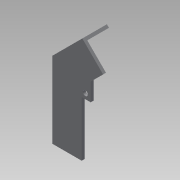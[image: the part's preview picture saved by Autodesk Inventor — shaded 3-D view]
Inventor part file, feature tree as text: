
AUTODESK INVENTOR PART (.ipt)
format: ipt  version: 2015 SP1 (Build 190203100, 203)  size: 113,152 bytes
history: native  units: mm
features: sketch x2, extrude x2, projected_geometry x1
ambient origin geometry x8: Origin, YZ Plane, XZ Plane, XY Plane, X Axis, Y Axis, Z Axis, Center Point
bodies: Body1 (feature_tree)
feature tree (5):
  sketch  "Sketch1"  dims[d18=2.0mm d19=0.0mm d20=15.0mm]
  extrude  "Extrusion3"  Depth=15.0mm
  extrude  "Extrusion4"  Depth=2.0mm
  sketch  "Sketch3"  dims[d21=90.0deg d22=2.0mm d23=15.0mm d24=90.0deg d25=2.0mm d26=15.0mm d27=45.0deg d28=2.0mm d29=7.5mm d30=2.0mm d31=15.0mm d32=0.0mm]
  projected_geometry  "Projected Loop1"
